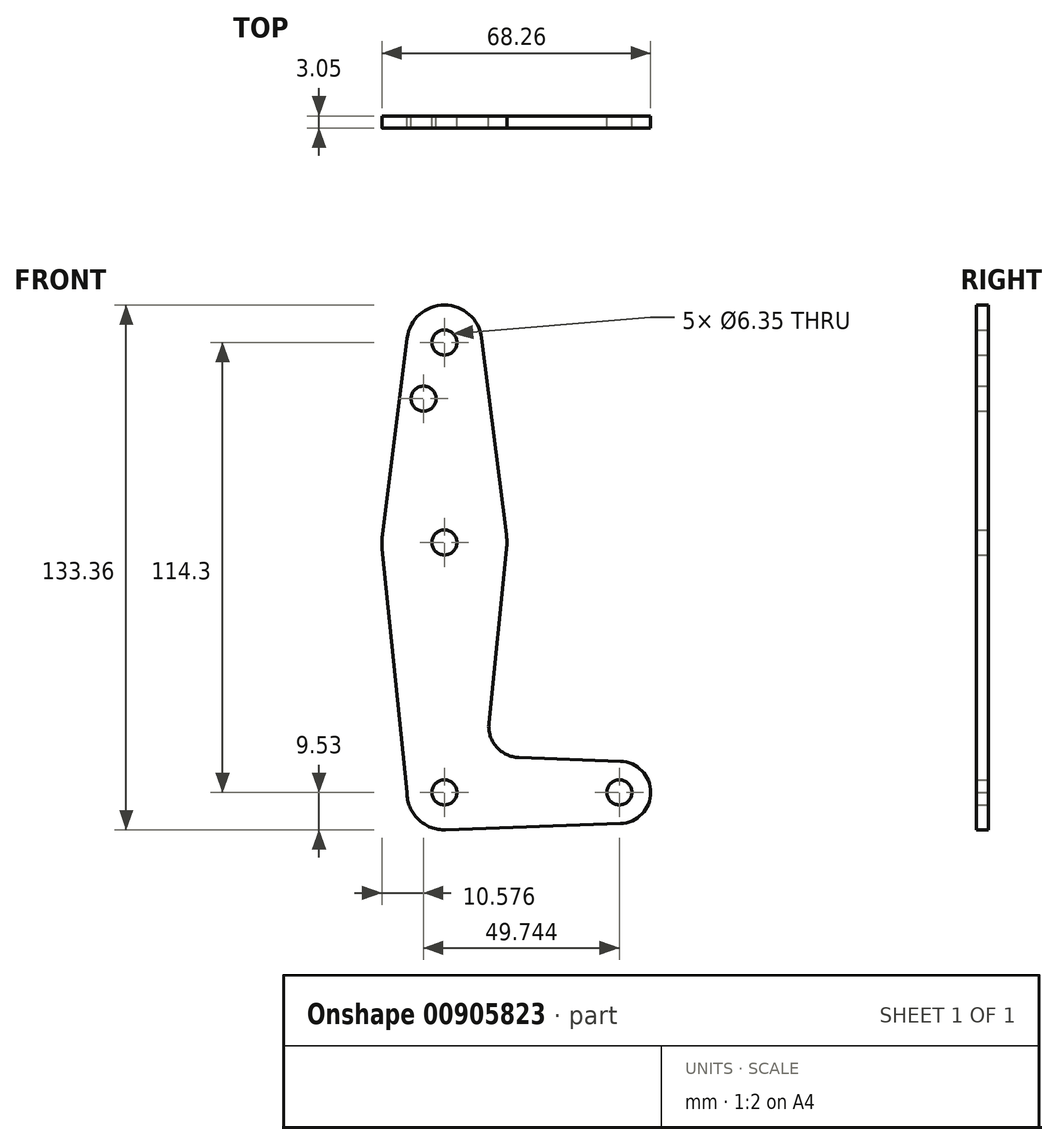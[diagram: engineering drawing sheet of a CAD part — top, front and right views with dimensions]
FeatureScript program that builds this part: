
annotation { "Feature Type Name" : "Feature", "Feature Type Description" : "" }
export const myFeature = defineFeature(function(context is Context, id is Id, definition is map)
    precondition{}
    {
        {
            var Q0;
            Q0=qCreatedBy(makeId("Front.planeOp"),FACE);
            var sketch = newSketch(context, id + "F0", { "sketchPlane" : qUnion([Q0])});
            skCircle(sketch, "E0", {"center": v(44.45, 0) * mm, "radius": 7.94 * mm});
            skCircle(sketch, "E1", {"center": v(0, 114.3) * mm, "radius": 9.53 * mm});
            skCircle(sketch, "E2", {"center": v(0, 63.5) * mm, "radius": 15.88 * mm});
            skCircle(sketch, "E3", {"center": v(0, 0) * mm, "radius": 9.53 * mm});
            skLineSegment(sketch, "E4", {"start": v(0, 0) * mm, "end": v(44.45, 0) * mm, "construction": true});
            skLineSegment(sketch, "E5", {"start": v(0, 0) * mm, "end": v(0, 114.3) * mm, "construction": true});
            skLineSegment(sketch, "E6", {"start": v(9.45, 115.5) * mm, "end": v(15.75, 65.48) * mm});
            skLineSegment(sketch, "E7", {"start": v(-9.45, 115.5) * mm, "end": v(-15.75, 65.48) * mm});
            skLineSegment(sketch, "E8", {"start": v(-9.52, 0) * mm, "end": v(-15.8, 61.9) * mm});
            skLineSegment(sketch, "E9", {"start": v(11.3, 17.6) * mm, "end": v(15.8, 61.9) * mm});
            skLineSegment(sketch, "E10", {"start": v(18.93, 8.85) * mm, "end": v(44.73, 7.93) * mm});
            skLineSegment(sketch, "E11", {"start": v(0.34, -9.52) * mm, "end": v(44.73, -7.93) * mm});
            skCircle(sketch, "E12", {"center": v(0, 114.3) * mm, "radius": 3.18 * mm});
            skCircle(sketch, "E13", {"center": v(44.45, 0) * mm, "radius": 3.18 * mm});
            skCircle(sketch, "E14", {"center": v(0, 63.5) * mm, "radius": 3.18 * mm});
            skCircle(sketch, "E15", {"center": v(0, 0) * mm, "radius": 3.18 * mm});
            skCircle(sketch, "E16", {"center": v(-5.3, 100.03) * mm, "radius": 3.18 * mm});
            skPoint(sketch, "E17.newPointB", {"position": v(9.53, 0) * mm});
            skArc(sketch, "E17.filletArc", {"start": v(11.3, 17.6) * mm, "mid": v(13.22, 11.57) * mm, "end": v(18.93, 8.85) * mm});
            skSolve(sketch);
        }
        {
            var Q0;
            Q0 = qSketchRegion(id + "F0", true);
            extrude(context, id + "F1", {"entities" : qUnion([Q0]), "depth" : 3.05 * mm, "offsetDistance" : 25.4 * mm});
        }
    });
